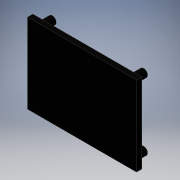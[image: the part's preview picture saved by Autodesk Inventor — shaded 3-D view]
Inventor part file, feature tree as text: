
AUTODESK INVENTOR PART (.ipt)
format: ipt  version: 2016 (Build 200138000, 138)  size: 139,264 bytes
history: native  units: mm
features: sketch x3, extrude x2, hole x1
ambient origin geometry x8: Origin, YZ Plane, XZ Plane, XY Plane, X Axis, Y Axis, Z Axis, Center Point
bodies: Solid1 (feature_tree)
feature tree (6):
  extrude  "Extrusion1"  Depth=45.0mm
  hole  "Hole1"  [1 undecoded]
  extrude  "Extrusion2"  Depth=6.0mm
  sketch  "Sketch1"  dims[d0=61.5mm d1=45.0mm]
  sketch  "Sketch2"  dims[d2=3.0mm d3=0.0mm d4=5.0mm]
  sketch  "Sketch3"  dims[d5=27.0mm d8=5.0mm d9=12.0mm d10=5.0mm d11=18.0mm d12=5.0mm d13=7.5mm d14=7.5mm d15=18.0mm d16=5.0mm d17=6.0mm d18=4.0mm d19=2.0mm d20=90.0deg d21=2.5mm d22=0.0mm d23=4.5mm d24=3.5mm d25=5.0mm d26=4.5mm d27=3.5mm d28=5.0mm d29=4.5mm d30=3.5mm d31=4.5mm d32=4.5mm d33=24.5mm d34=5.0mm d35=5.0mm d36=3.5mm d37=4.5mm d38=20.0mm d39=6.0mm d40=0.0mm]
note: 1 required parameter value undecoded (feature->parameter linkage not recoverable at this tier; creation-order binding heuristic only, values carry confidence <= 0.55)
